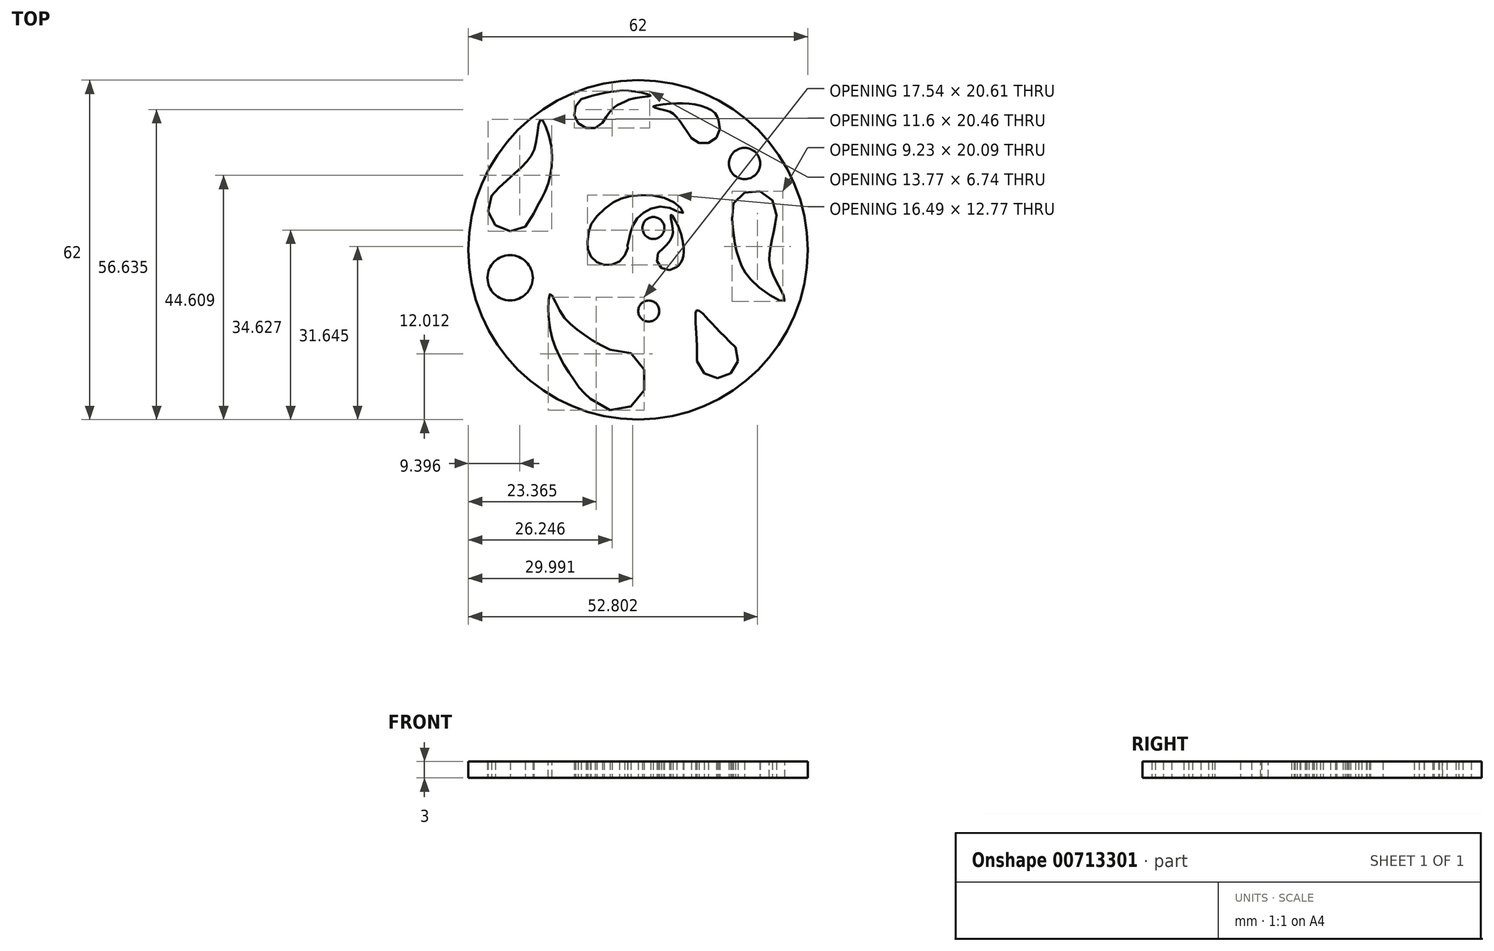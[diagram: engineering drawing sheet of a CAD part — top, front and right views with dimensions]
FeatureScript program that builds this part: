
annotation { "Feature Type Name" : "Feature", "Feature Type Description" : "" }
export const myFeature = defineFeature(function(context is Context, id is Id, definition is map)
    precondition{}
    {
        {
            var Q0;
            Q0=qCreatedBy(makeId("Top.planeOp"),FACE);
            var sketch = newSketch(context, id + "F0", { "sketchPlane" : qUnion([Q0])});
            skCircle(sketch, "E0", {"center": v(0.2, 0.4) * mm, "radius": 31 * mm});
            skCircle(sketch, "E1", {"center": v(2.99, 4.39) * mm, "radius": 2 * mm});
            skArc(sketch, "E2.cCircle", {"start": v(-9.04, 1.2) * mm, "mid": v(-6, -2.3) * mm, "end": v(-1.97, 0.01) * mm, "construction": true});
            skLineSegment(sketch, "E2.2", {"start": v(-1.71, 0.7) * mm, "end": v(-2.23, -0.67) * mm});
            skLineSegment(sketch, "E2.3", {"start": v(-2.23, -0.67) * mm, "end": v(-3.22, -1.73) * mm});
            skLineSegment(sketch, "E2.4", {"start": v(-3.22, -1.73) * mm, "end": v(-4.55, -2.32) * mm});
            skLineSegment(sketch, "E2.5", {"start": v(-4.55, -2.32) * mm, "end": v(-6, -2.37) * mm});
            skLineSegment(sketch, "E2.6", {"start": v(-6, -2.37) * mm, "end": v(-7.36, -1.85) * mm});
            skLineSegment(sketch, "E2.7", {"start": v(-7.36, -1.85) * mm, "end": v(-8.42, -0.86) * mm});
            skLineSegment(sketch, "E2.8", {"start": v(-8.42, -0.86) * mm, "end": v(-9.02, 0.47) * mm});
            skLineSegment(sketch, "E2.9", {"start": v(-9.02, 0.47) * mm, "end": v(-9.06, 1.92) * mm});
            skFitSpline(sketch, "E3", {"points": [v(-9.06, 1.92) * mm, v(-8.19, 5.36) * mm, v(-4.75, 8.85) * mm, v(-1.3, 10.19) * mm, v(4.54, 10.04) * mm, v(8.09, 7.88) * mm, v(8.34, 7.06) * mm, v(5.52, 8.19) * mm, v(1.87, 7.62) * mm, v(-0.44, 5.52) * mm, v(-1.3, 3.18) * mm, v(-1.73, 1.2) * mm], "startDerivative": vector(7.71, 51.87) * mm, "endDerivative": vector(-9.59, -37.13) * mm});
            skFitSpline(sketch, "E4", {"points": [v(-1.73, 1.22) * mm, v(-1.71, 0.7) * mm], "startDerivative": vector(0.02, -0.53) * mm, "endDerivative": vector(0.02, -0.53) * mm});
            skArc(sketch, "E5.cCircle", {"start": v(4.37, 0.3) * mm, "mid": v(4.08, -2.3) * mm, "end": v(6.59, -3.04) * mm, "construction": true});
            skLineSegment(sketch, "E5.1", {"start": v(7.26, -2.74) * mm, "end": v(5.9, -3.34) * mm});
            skLineSegment(sketch, "E5.2", {"start": v(5.9, -3.34) * mm, "end": v(4.49, -2.92) * mm});
            skLineSegment(sketch, "E5.3", {"start": v(4.49, -2.92) * mm, "end": v(3.67, -1.69) * mm});
            skLineSegment(sketch, "E5.4", {"start": v(3.67, -1.69) * mm, "end": v(3.84, -0.22) * mm});
            skLineSegment(sketch, "E5.5", {"start": v(3.84, -0.22) * mm, "end": v(4.83, 0.74) * mm});
            skFitSpline(sketch, "E6", {"points": [v(4.83, 0.74) * mm, v(6.38, 2.76) * mm, v(6.38, 5.11) * mm, v(6.24, 6.83) * mm, v(7.73, 4.24) * mm, v(8.24, 2.44) * mm, v(8.43, 1.37) * mm, v(8.53, -0.45) * mm, v(7.92, -2.08) * mm, v(7.26, -2.74) * mm], "startDerivative": vector(14.1, 13.13) * mm, "endDerivative": vector(-9.01, -6.55) * mm});
            skArc(sketch, "E7.cCircle", {"start": v(-10.03, 23.09) * mm, "mid": v(-8.75, 22.68) * mm, "end": v(-7.42, 22.91) * mm, "construction": true});
            skLineSegment(sketch, "E7.1", {"start": v(-6.31, 23.6) * mm, "end": v(-7.69, 22.68) * mm});
            skLineSegment(sketch, "E7.2", {"start": v(-7.69, 22.68) * mm, "end": v(-9.34, 22.66) * mm});
            skLineSegment(sketch, "E7.3", {"start": v(-9.34, 22.66) * mm, "end": v(-10.74, 23.52) * mm});
            skLineSegment(sketch, "E7.4", {"start": v(-10.74, 23.52) * mm, "end": v(-11.45, 25.01) * mm});
            skLineSegment(sketch, "E7.5", {"start": v(-11.45, 25.01) * mm, "end": v(-11.24, 26.65) * mm});
            skLineSegment(sketch, "E7.6", {"start": v(-11.24, 26.65) * mm, "end": v(-10.18, 27.91) * mm});
            skFitSpline(sketch, "E8", {"points": [v(-10.18, 27.91) * mm, v(-7.06, 28.83) * mm, v(-3.36, 29.45) * mm, v(0.2, 29.23) * mm, v(2.48, 28.54) * mm, v(-0.28, 28.16) * mm, v(-2.64, 27.31) * mm, v(-4.12, 26.48) * mm, v(-6.31, 23.6) * mm], "startDerivative": vector(21.94, 8.94) * mm, "endDerivative": vector(-14.57, -25.46) * mm});
            skArc(sketch, "E9.cCircle", {"start": v(10.62, 20.38) * mm, "mid": v(13.76, 20.41) * mm, "end": v(15.04, 23.28) * mm, "construction": true});
            skLineSegment(sketch, "E9.0", {"start": v(15.17, 22.44) * mm, "end": v(14.48, 20.88) * mm});
            skLineSegment(sketch, "E9.1", {"start": v(14.48, 20.88) * mm, "end": v(13.05, 19.94) * mm});
            skLineSegment(sketch, "E9.2", {"start": v(13.05, 19.94) * mm, "end": v(11.35, 19.92) * mm});
            skLineSegment(sketch, "E9.3", {"start": v(11.35, 19.92) * mm, "end": v(9.9, 20.83) * mm});
            skLineSegment(sketch, "E9.10", {"start": v(14.9, 24.13) * mm, "end": v(15.17, 22.44) * mm});
            skFitSpline(sketch, "E10", {"points": [v(9.9, 20.83) * mm, v(7.2, 24.72) * mm, v(5.38, 25.84) * mm, v(2.92, 26.53) * mm, v(6.12, 27.1) * mm, v(10.46, 26.99) * mm, v(14, 25.64) * mm, v(14.9, 24.13) * mm], "startDerivative": vector(-16.43, 25.81) * mm, "endDerivative": vector(5.43, -14.93) * mm});
            skCircle(sketch, "E11", {"center": v(19.65, 16.17) * mm, "radius": 2.86 * mm});
            skLineSegment(sketch, "E12.4", {"start": v(17.38, 6.05) * mm, "end": v(17.64, 8.86) * mm});
            skLineSegment(sketch, "E12.5", {"start": v(17.64, 8.86) * mm, "end": v(19.64, 10.85) * mm});
            skLineSegment(sketch, "E12.6", {"start": v(19.64, 10.85) * mm, "end": v(22.45, 11.08) * mm});
            skLineSegment(sketch, "E12.7", {"start": v(22.45, 11.08) * mm, "end": v(24.76, 9.45) * mm});
            skLineSegment(sketch, "E12.8", {"start": v(24.76, 9.45) * mm, "end": v(25.47, 6.72) * mm});
            skFitSpline(sketch, "E13", {"points": [v(17.38, 6.05) * mm, v(17.84, 1.78) * mm, v(18.88, -1.96) * mm, v(21.46, -5.75) * mm, v(26.94, -8.94) * mm, v(24.81, -4.1) * mm, v(24.2, -0.59) * mm, v(24.74, 2.61) * mm, v(25.47, 6.72) * mm], "startDerivative": vector(2.51, -34.81) * mm, "endDerivative": vector(5.4, 38.44) * mm});
            skArc(sketch, "E14.cCircle", {"start": v(-26.9, 8.86) * mm, "mid": v(-26.96, 7.47) * mm, "end": v(-26.54, 6.15) * mm, "construction": true});
            skLineSegment(sketch, "E14.0", {"start": v(-18.85, 7.11) * mm, "end": v(-20.4, 4.65) * mm});
            skLineSegment(sketch, "E14.1", {"start": v(-20.4, 4.65) * mm, "end": v(-23.17, 3.77) * mm});
            skLineSegment(sketch, "E14.2", {"start": v(-23.17, 3.77) * mm, "end": v(-25.86, 4.87) * mm});
            skLineSegment(sketch, "E14.3", {"start": v(-25.86, 4.87) * mm, "end": v(-27.21, 7.44) * mm});
            skLineSegment(sketch, "E14.4", {"start": v(-27.21, 7.44) * mm, "end": v(-26.6, 10.28) * mm});
            skFitSpline(sketch, "E15", {"points": [v(-18.85, 7.11) * mm, v(-16.35, 12.17) * mm, v(-15.74, 19.68) * mm, v(-17.57, 24.23) * mm, v(-18.43, 20.12) * mm, v(-20.39, 16.2) * mm, v(-26.6, 10.28) * mm], "startDerivative": vector(15.26, 31.78) * mm, "endDerivative": vector(-29.52, -34.24) * mm});
            skArc(sketch, "E16.trimOffspring", {"start": v(-21.79, 4.21) * mm, "mid": v(-21.5, 4.32) * mm, "end": v(-21.22, 4.44) * mm, "construction": true});
            skCircle(sketch, "E17", {"center": v(-23.2, -4.72) * mm, "radius": 4.14 * mm});
            skArc(sketch, "E18.cCircle", {"start": v(-6.58, -27.94) * mm, "mid": v(1, -25.18) * mm, "end": v(-3.03, -18.19) * mm, "construction": true});
            skLineSegment(sketch, "E18.0", {"start": v(1.32, -21.46) * mm, "end": v(1.32, -25.3) * mm});
            skLineSegment(sketch, "E18.1", {"start": v(1.32, -25.3) * mm, "end": v(-1.14, -28.23) * mm});
            skLineSegment(sketch, "E18.2", {"start": v(-1.14, -28.23) * mm, "end": v(-4.92, -28.9) * mm});
            skLineSegment(sketch, "E18.3", {"start": v(-4.92, -28.9) * mm, "end": v(-8.52, -26.82) * mm});
            skLineSegment(sketch, "E18.7", {"start": v(-4.92, -17.85) * mm, "end": v(-1.14, -18.52) * mm});
            skLineSegment(sketch, "E18.8", {"start": v(-1.14, -18.52) * mm, "end": v(1.32, -21.46) * mm});
            skFitSpline(sketch, "E19", {"points": [v(-4.92, -17.85) * mm, v(-10.61, -14.43) * mm, v(-14.13, -10.74) * mm, v(-15.83, -7.63) * mm, v(-16.17, -11.85) * mm, v(-14.72, -17.85) * mm, v(-11.6, -23.3) * mm, v(-8.52, -26.82) * mm], "startDerivative": vector(-38.38, 16.46) * mm, "endDerivative": vector(25.55, -19.41) * mm});
            skArc(sketch, "E20.cCircle", {"start": v(11.62, -21.06) * mm, "mid": v(16.98, -22) * mm, "end": v(16.98, -16.57) * mm, "construction": true});
            skLineSegment(sketch, "E20.1", {"start": v(16.98, -16.57) * mm, "end": v(17.97, -17.4) * mm});
            skLineSegment(sketch, "E20.2", {"start": v(17.97, -17.4) * mm, "end": v(18.42, -19.94) * mm});
            skLineSegment(sketch, "E20.3", {"start": v(18.42, -19.94) * mm, "end": v(17.12, -22.18) * mm});
            skLineSegment(sketch, "E20.4", {"start": v(17.12, -22.18) * mm, "end": v(14.7, -23.06) * mm});
            skLineSegment(sketch, "E20.5", {"start": v(14.7, -23.06) * mm, "end": v(12.27, -22.18) * mm});
            skLineSegment(sketch, "E20.6", {"start": v(12.27, -22.18) * mm, "end": v(10.98, -19.94) * mm});
            skFitSpline(sketch, "E21", {"points": [v(10.98, -19.94) * mm, v(10.98, -10.67) * mm, v(17.97, -17.4) * mm], "startDerivative": vector(0, 34.67) * mm, "endDerivative": vector(24.65, -23.22) * mm});
            skCircle(sketch, "E22", {"center": v(2.14, -10.8) * mm, "radius": 1.93 * mm});
            skSolve(sketch);
        }
        {
            var Q0;
            Q0=makeQuery(id+"F0.imprint","IMPRINT",FACE,{"disambiguationData":[TD([[makeQuery(id+"F0.imprint","IMPRINT",EDGE,{"derivedFrom":sQuery(id+"F0.wireOp",EDGE,"E0")}),1.0]])]});
            extrude(context, id + "F1", {"entities" : qUnion([Q0]), "depth" : 3 * mm, "offsetDistance" : 25.4 * mm});
        }
    });
